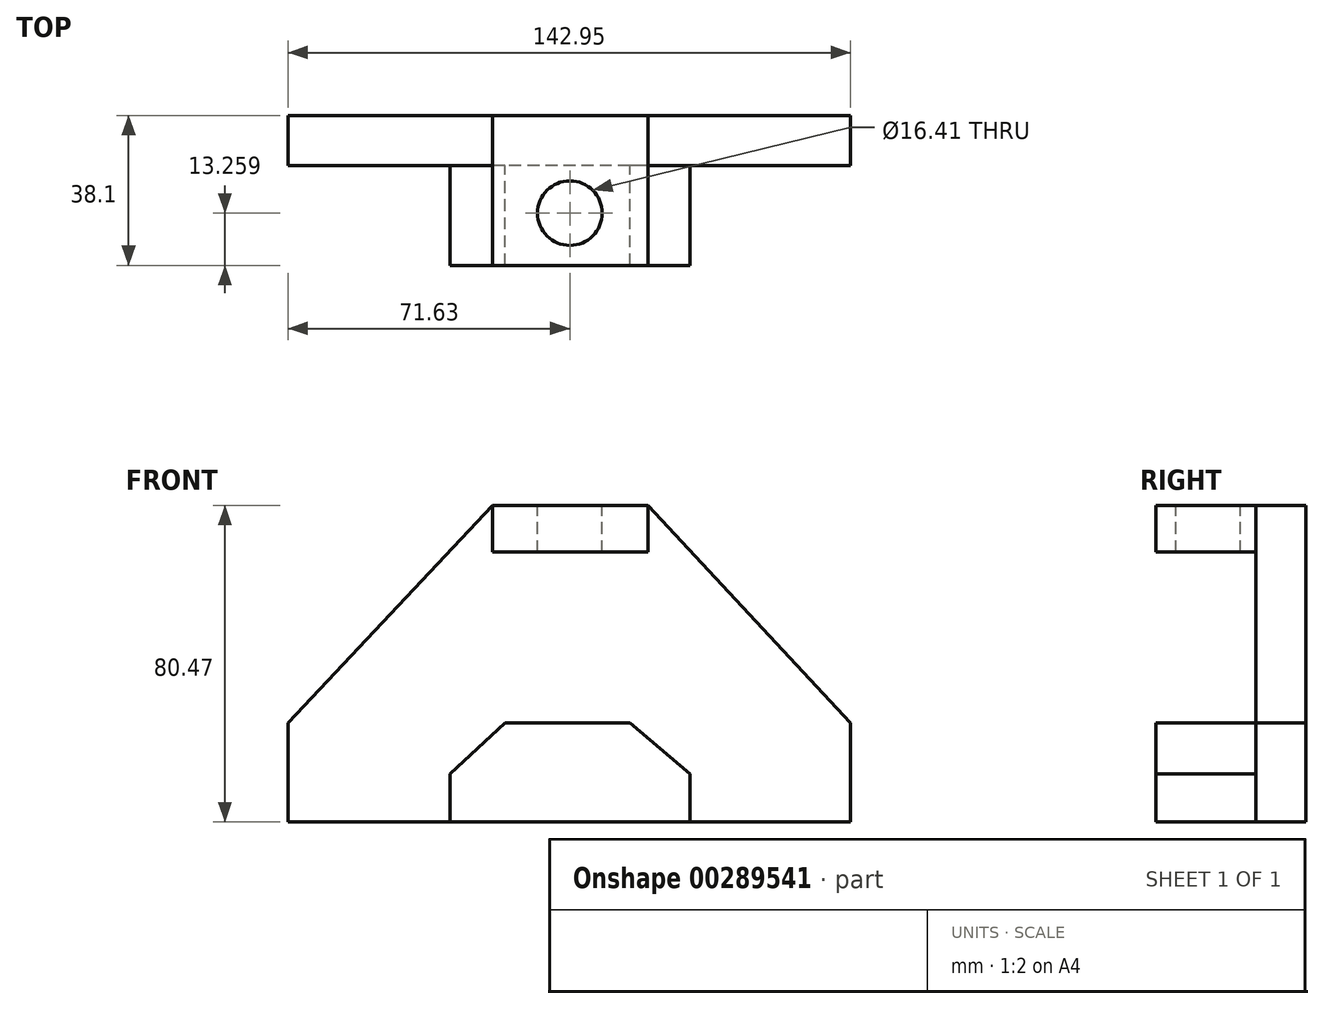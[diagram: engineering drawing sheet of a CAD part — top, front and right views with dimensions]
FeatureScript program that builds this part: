
annotation { "Feature Type Name" : "Feature", "Feature Type Description" : "" }
export const myFeature = defineFeature(function(context is Context, id is Id, definition is map)
    precondition{}
    {
        {
            var Q0;
            Q0=qCreatedBy(makeId("Front.planeOp"),FACE);
            var sketch = newSketch(context, id + "F0", { "sketchPlane" : qUnion([Q0])});
            skLineSegment(sketch, "E0", {"start": v(-71.63, -25.15) * mm, "end": v(71.32, -25.15) * mm});
            skLineSegment(sketch, "E1", {"start": v(71.32, -25.15) * mm, "end": v(71.32, 0) * mm});
            skLineSegment(sketch, "E2", {"start": v(71.32, 0) * mm, "end": v(19.81, 55.32) * mm});
            skLineSegment(sketch, "E3", {"start": v(-71.63, -25.15) * mm, "end": v(-71.63, 0) * mm});
            skLineSegment(sketch, "E4", {"start": v(-71.63, 0) * mm, "end": v(-19.66, 55.32) * mm});
            skLineSegment(sketch, "E5", {"start": v(-19.66, 55.32) * mm, "end": v(19.81, 55.32) * mm});
            skSolve(sketch);
        }
        {
            var Q0;
            Q0=makeQuery(id+"F0.imprint","IMPRINT",FACE,{"disambiguationData":[TD([[makeQuery(id+"F0.imprint","IMPRINT",EDGE,{"derivedFrom":sQuery(id+"F0.wireOp",EDGE,"E0")}),1.0]])]});
            extrude(context, id + "F1", {"entities" : qUnion([Q0]), "depth" : 12.7 * mm});
        }
        {
            var Q0;
            Q0=makeQuery(id+"F1.opExtrude","CAP_FACE",FACE,{"disambiguationData":[OSD([sQuery(id+"F0.wireOp",EDGE,"E0"),sQuery(id+"F0.wireOp",EDGE,"E1"),sQuery(id+"F0.wireOp",EDGE,"E2"),sQuery(id+"F0.wireOp",EDGE,"E3"),sQuery(id+"F0.wireOp",EDGE,"E4"),sQuery(id+"F0.wireOp",EDGE,"E5")])],"isStart":false});
            var sketch = newSketch(context, id + "F2", { "sketchPlane" : qUnion([Q0])});
            skLineSegment(sketch, "E6", {"start": v(-19.66, 55.32) * mm, "end": v(19.81, 55.32) * mm});
            skLineSegment(sketch, "E7", {"start": v(19.81, 55.32) * mm, "end": v(19.81, 43.48) * mm});
            skLineSegment(sketch, "E8", {"start": v(19.81, 43.48) * mm, "end": v(-19.66, 43.48) * mm});
            skLineSegment(sketch, "E9", {"start": v(-19.66, 43.48) * mm, "end": v(-19.66, 55.32) * mm});
            skSolve(sketch);
        }
        {
            var Q0;
            Q0=makeQuery(id+"F2.imprint","IMPRINT",FACE,{"disambiguationData":[TD([[makeQuery(id+"F2.imprint","IMPRINT",EDGE,{"derivedFrom":sQuery(id+"F2.wireOp",EDGE,"E6")}),-1.0]])]});
            extrude(context, id + "F3", {"entities" : qUnion([Q0]), "operationType" : NewBodyOperationType.ADD, "depth" : 25.4 * mm});
        }
        {
            var Q0;
            Q0=makeQuery(id+"F3.boolean.opBoolean","MERGE",FACE,{"derivedFrom":[makeQuery(id+"F1.opExtrude","SWEPT_FACE",FACE,{"disambiguationData":[OSD([sQuery(id+"F0.wireOp",EDGE,"E5")])]}),makeQuery(id+"F3.opExtrude","SWEPT_FACE",FACE,{"disambiguationData":[OSD([sQuery(id+"F2.wireOp",EDGE,"E6")])]})]});
            var sketch = newSketch(context, id + "F4", { "sketchPlane" : qUnion([Q0])});
            skCircle(sketch, "E10", {"center": v(0, -24.84) * mm, "radius": 8.2 * mm});
            skSolve(sketch);
        }
        {
            var Q0;
            Q0 = qSketchRegion(id + "F4", true);
            extrude(context, id + "F5", {"entities" : qUnion([Q0]), "operationType" : NewBodyOperationType.REMOVE, "oppositeDirection" : true, "depth" : 25.4 * mm});
        }
        {
            var Q0;
            Q0=makeQuery(id+"F1.opExtrude","CAP_FACE",FACE,{"disambiguationData":[OSD([sQuery(id+"F0.wireOp",EDGE,"E0"),sQuery(id+"F0.wireOp",EDGE,"E1"),sQuery(id+"F0.wireOp",EDGE,"E2"),sQuery(id+"F0.wireOp",EDGE,"E3"),sQuery(id+"F0.wireOp",EDGE,"E4"),sQuery(id+"F0.wireOp",EDGE,"E5")])],"isStart":false});
            var sketch = newSketch(context, id + "F6", { "sketchPlane" : qUnion([Q0])});
            skLineSegment(sketch, "E11", {"start": v(30.48, -25.15) * mm, "end": v(30.48, -12.95) * mm});
            skLineSegment(sketch, "E12", {"start": v(30.48, -12.95) * mm, "end": v(15.24, 0) * mm});
            skLineSegment(sketch, "E13", {"start": v(15.24, 0) * mm, "end": v(-16.46, 0) * mm});
            skLineSegment(sketch, "E14", {"start": v(-16.46, 0) * mm, "end": v(-30.48, -12.95) * mm});
            skLineSegment(sketch, "E15", {"start": v(-30.48, -12.95) * mm, "end": v(-30.48, -25.15) * mm});
            skLineSegment(sketch, "E16", {"start": v(-30.48, -25.15) * mm, "end": v(30.48, -25.15) * mm});
            skSolve(sketch);
        }
        {
            var Q0;
            Q0 = qSketchRegion(id + "F6", true);
            extrude(context, id + "F7", {"entities" : qUnion([Q0]), "operationType" : NewBodyOperationType.ADD, "depth" : 25.4 * mm});
        }
    });
